# Revit family: Коробка соединительная
name_source: partatom
category: Электрооборудование
units: mm (PartAtom-declared; Revit-internal decimal feet)

## family parameters
Всегда вертикально = Да
Заголовок OmniClass = Communication and Data Processing Equipment
Конфигурация панели = Два столбца, слева направо
На основе рабочей плоскости = Нет
Номер OmniClass = 23.85.50.17
Общий = Нет
При загрузке вырезать с полостями = Нет
Размер круглого соединителя = Использовать диаметр
Тип детали = Щит
Точка расчета площади = Нет

## types (4) — shared parameters
ADSK_Единица измерения = шт.
ADSK_Завод-изготовитель = НПП «МАГНИТО-КОНТАКТ»
URL = https://m-kontakt.ru
Изготовитель = НПП «МАГНИТО-КОНТАКТ»
Цвет = Металл

## per-type parameters (varying)
| type | ADSK_Код изделия | ADSK_Масса | ADSK_Наименование | Мороз | Описание | С выводами | Северленд |
| МКС «МОРОЗ» глухая | 00-00005375 | 0.47 | МКС «МОРОЗ» | Да | МКС «МОРОЗ» IP66/IP68 "глухая", корпус из алюминиевого сплава. | Нет | Нет |
| МКС «МОРОЗ» с вводами | 00-00005377 | 0.49 | МКС «МОРОЗ» IP66/IP68 с пластиковыми вводами | Да | МКС «МОРОЗ» IP66/IP68 с 2-мя пластиковыми вводами, корпус из алюминиевого сплава | Да | Нет |
| Ех коробка металлическая «СЕВЕРЛЕНД» с резьбой | 00-00003797 | 1.26 | Ех коробка металлическая «СЕВЕРЛЕНД» с резьбой | Нет | Маркировка взрывозащиты  1Ех db IIC T6...T3 Gb.   Корпус из алюминиевого сплава,С резьбой под 4 кабельных ввода . | Нет | Да |
| Ех коробка металлическая «СЕВЕРЛЕНД» с вводами | 00-00005744 | 1.86 | Ех коробка металлическая «СЕВЕРЛЕНД» с вводами | Нет | Маркировка взрывозащиты 1Ех db IIC T6...T3 Gb.  Корпус из алюминиевого сплава, с 4 кабельными вводами. | Да | Да |
